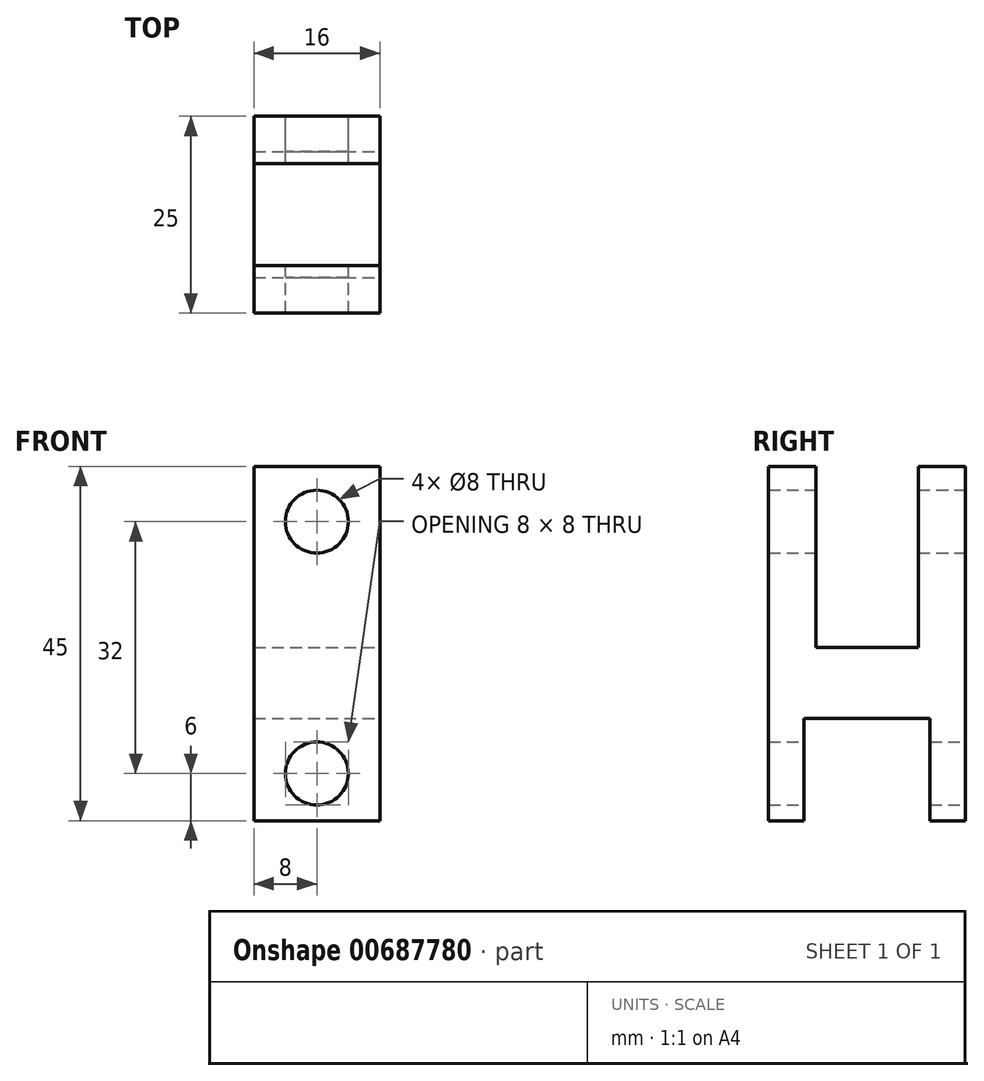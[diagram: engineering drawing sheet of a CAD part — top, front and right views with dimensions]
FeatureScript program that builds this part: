
annotation { "Feature Type Name" : "Feature", "Feature Type Description" : "" }
export const myFeature = defineFeature(function(context is Context, id is Id, definition is map)
    precondition{}
    {
        {
            var Q0;
            Q0=qCreatedBy(makeId("Front.planeOp"),FACE);
            var sketch = newSketch(context, id + "F0", { "sketchPlane" : qUnion([Q0])});
            skCircle(sketch, "E0", {"center": v(0, 6) * mm, "radius": 4 * mm});
            skLineSegment(sketch, "E1.bottom", {"start": v(-8, 0) * mm, "end": v(8, 0) * mm});
            skLineSegment(sketch, "E1.top", {"start": v(-8, 45) * mm, "end": v(8, 45) * mm});
            skLineSegment(sketch, "E1.left", {"start": v(-8, 0) * mm, "end": v(-8, 45) * mm});
            skLineSegment(sketch, "E1.right", {"start": v(8, 0) * mm, "end": v(8, 45) * mm});
            skCircle(sketch, "E2", {"center": v(0, 38) * mm, "radius": 4 * mm});
            skSolve(sketch);
        }
        {
            var Q0;
            Q0 = qSketchRegion(id + "F0", true);
            extrude(context, id + "F1", {"entities" : qUnion([Q0]), "depth" : 25 * mm, "offsetDistance" : 25 * mm});
        }
        {
            var Q0;
            Q0=makeQuery(id+"F1.opExtrude","SWEPT_FACE",FACE,{"disambiguationData":[OSD([sQuery(id+"F0.wireOp",EDGE,"E1.right")])]});
            var sketch = newSketch(context, id + "F2", { "sketchPlane" : qUnion([Q0])});
            skLineSegment(sketch, "E3.bottom", {"start": v(-20.5, 0) * mm, "end": v(-4.5, 0) * mm});
            skLineSegment(sketch, "E3.top", {"start": v(-20.5, 13) * mm, "end": v(-4.5, 13) * mm});
            skLineSegment(sketch, "E3.left", {"start": v(-20.5, 0) * mm, "end": v(-20.5, 13) * mm});
            skLineSegment(sketch, "E3.right", {"start": v(-4.5, 0) * mm, "end": v(-4.5, 13) * mm});
            skLineSegment(sketch, "E4.bottom", {"start": v(-19, 45) * mm, "end": v(-6, 45) * mm});
            skLineSegment(sketch, "E4.top", {"start": v(-19, 22) * mm, "end": v(-6, 22) * mm});
            skLineSegment(sketch, "E4.left", {"start": v(-19, 45) * mm, "end": v(-19, 22) * mm});
            skLineSegment(sketch, "E4.right", {"start": v(-6, 45) * mm, "end": v(-6, 22) * mm});
            skSolve(sketch);
        }
        {
            var Q0;
            Q0=makeQuery(id+"F2.imprint","IMPRINT",FACE,{"disambiguationData":[TD([[makeQuery(id+"F2.imprint","IMPRINT",EDGE,{"derivedFrom":sQuery(id+"F2.wireOp",EDGE,"E3.bottom")}),1.0]])]});
            var Q1;
            Q1=makeQuery(id+"F2.imprint","IMPRINT",FACE,{"disambiguationData":[TD([[makeQuery(id+"F2.imprint","IMPRINT",EDGE,{"derivedFrom":sQuery(id+"F2.wireOp",EDGE,"E4.bottom")}),-1.0]])]});
            extrude(context, id + "F3", {"entities" : qUnion([Q0, Q1]), "operationType" : NewBodyOperationType.REMOVE, "endBound" : BoundingType.THROUGH_ALL, "oppositeDirection" : true, "depth" : 25 * mm, "offsetDistance" : 25 * mm});
        }
    });
